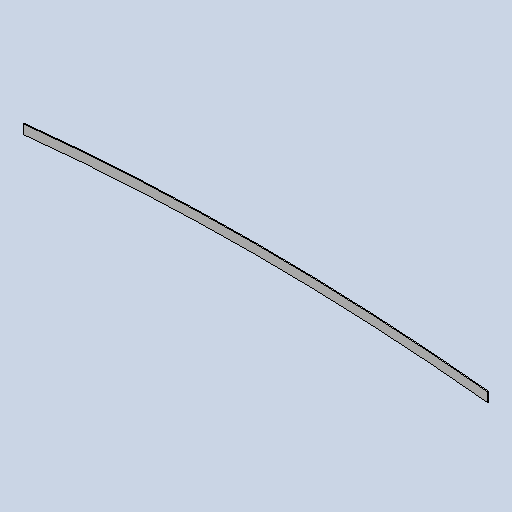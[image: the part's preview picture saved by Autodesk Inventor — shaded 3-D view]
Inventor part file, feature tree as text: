
AUTODESK INVENTOR PART (.ipt)
format: ipt  version: 2025 (Build 290162010, 162A)  size: 151,040 bytes
history: native  units: mm
features: other x2, sheet_metal_op x1, sketch x1
ambient origin geometry x8: Origin, YZ Plane, XZ Plane, XY Plane, X Axis, Y Axis, Z Axis, Center Point
bodies: Body1 (feature_tree)
feature tree (4):
  sheet_metal_op  "Face1"
  sketch  "Sketch5"  dims[d21=8688.265625mm d30=7200.0mm d31=30.0mm d32=1500.0mm d33=3.0mm]
  other  "Plate2"
  other  "Definition1"
